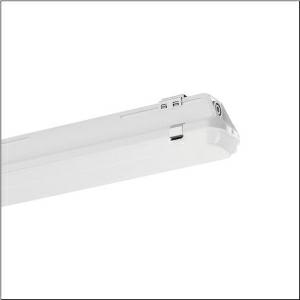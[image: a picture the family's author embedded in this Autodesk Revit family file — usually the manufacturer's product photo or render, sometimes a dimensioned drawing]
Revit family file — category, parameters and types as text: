
# Revit family: monsun_11_parking_51fg207p440h
name_source: partatom
category: Lighting Fixtures
units: mm (PartAtom-declared; Revit-internal decimal feet)

## family parameters
Cut with Voids When Loaded = No
Host = Face
Light Source = No
Part Type = Normal
Room Calculation Point = No
Round Connector Dimension = Use Diameter
Shared = No

## types (1)
- Monsun 11 parking (1 x LED, 4820 lm, 29.2 W, 4000K)
    Apparent Load = 29 VA
    CIE Flux Codes = 45 75 93 94 100
    Color Rendering = 80
    Color Temperature = 4000K
    Default Elevation = 1800 mm
    Description = Monsun 11 parking, damp-proof luminaire, chain hanger, primary optical cover: enclosure, of PC, light emission: direct distribution, primary light characteristic: symmetric, installation type: suspended mounting, surface-mounted, horizontal mounting, vertical mounting, LED, rated luminous flux: 4.820lm, luminous efficacy: 165lm/W, light colour: 840, colour temperature: 4000K, control gear: ON/OFF, with terminal, 3-pole, max. 2.5mm², mains connection: 220..240V, AC, 50/60Hz, rated input power: 29W, housing, of glass-fibre reinforced polyester, uncoated, bright grey, incl. chain hanger, length: 1.590mm, width: 90mm, height: 88mm, clip for enclosure, of stainless steel (V2A), ceiling mounting element, of stainless steel (V2A), chain hanger, of stainless steel (V2A), protection rating (complete): IP66, insulation class (complete): insulation class I (protective earthing), certification: CE, ENEC, VDE, UKCA, protection symbol: D, impact resistance: IK08, permissible operating ambient temperature: -35..+40°C, standard: EN 50419, EN 60598-2-1, no direct snow, no direct sun, no direct rain, for indoor or canopied outdoor use, corresponds to IFS (International Featured Standards) requirements for safety and quality in the food industry, contact your sales advisor before using the luminaires in applications with unclear chemical exposure, large temperature fluctuations or condensation-forming humidity, LABS conformity tested according to VDMA 24364:2018-05, packaging unit: 1 piece
    Height = 89 mm
    Lamp = 1 x LED
    Lamp Light Flux = 4820 lm
    Lamp Power = 29.2 W
    Lamp count = 1
    Length = 1590 mm
    Luminous efficacy = 165 lm/W
    Manufacturer = Siteco
    ModVariant = No
    Model = 51FG207P440H
    Mounting Place = Ceiling
    Mounting Type = Surface mounted
    Number of Poles = 1
    OnlyDefault = Yes
    Power Factor = 1
    Product Name = Monsun 11 parking
    Product group = damp-proof luminaire
    ProductGroupID = 300
    Protection Class = Protection class I
    Protection Degree = IP 66
    RLX_Detail_Level = 1
    RLX_Emergency_Light_Flux = 0 lm
    RLX_Emergency_Type = 0
    RLX_Emergency_Type_DB = No
    RlxData = <blob elided: 88337 chars, md5=463738e8>
    Socket = socket
    Standby Power = 0 W
    System Light Flux = 4820 lm
    System Power = 29 W
    Type Comments = Product without accessories
    Type Image = l_1349237.jpg
    URL = http://relux.com
    VarID = ---
    Voltage = 0 V
    Weight = 0.00 kg
    Width = 90 mm

## geometry (parser evidence)
native form markers: Blend x4, Sweep x11
no freeform markers — native parametric forms only
